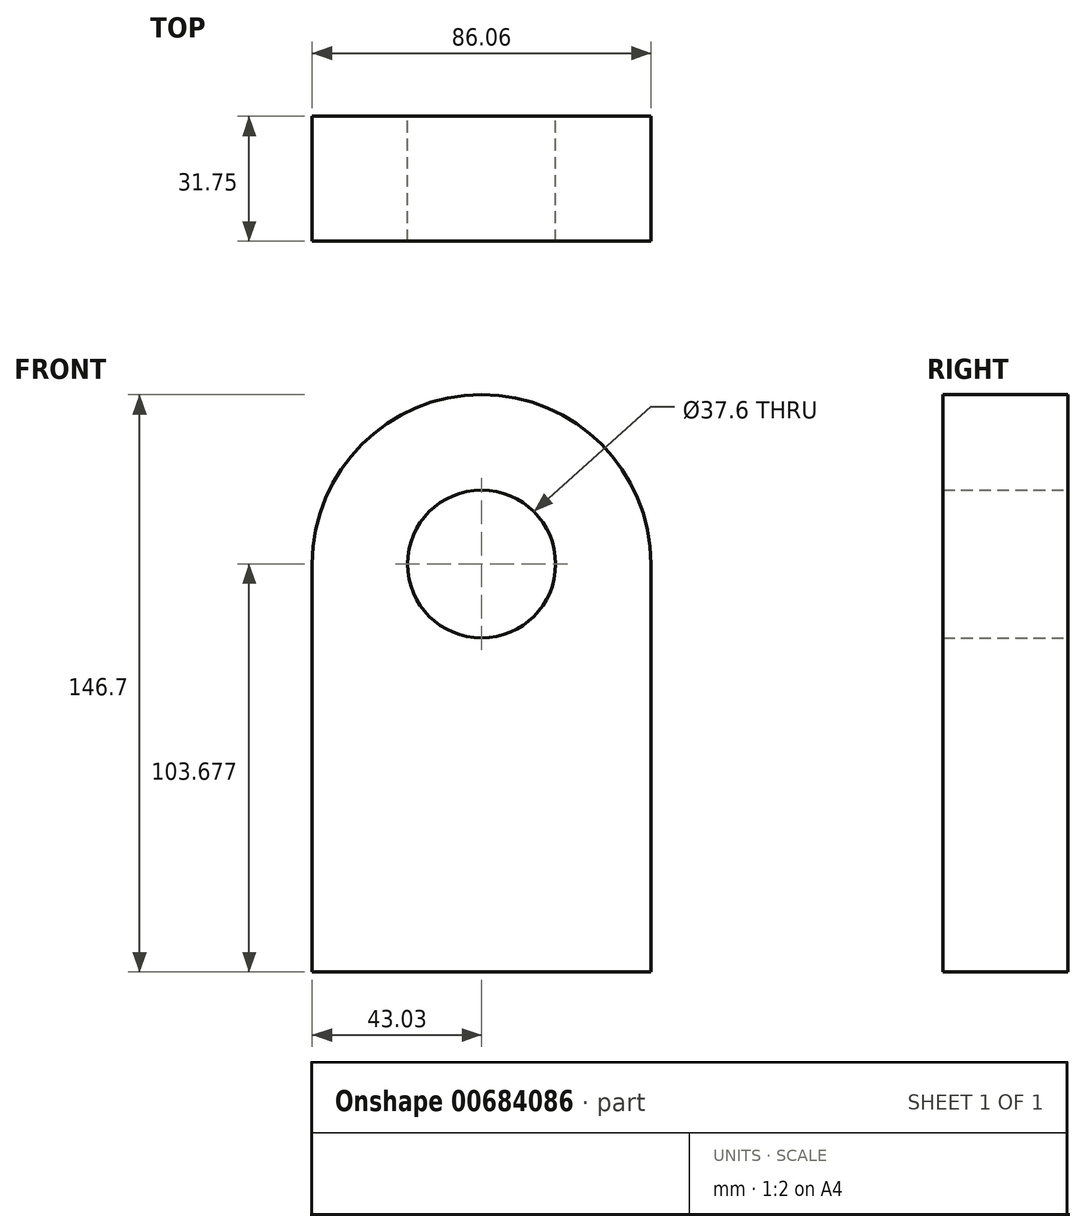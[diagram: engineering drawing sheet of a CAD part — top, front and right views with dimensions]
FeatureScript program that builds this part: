
annotation { "Feature Type Name" : "Feature", "Feature Type Description" : "" }
export const myFeature = defineFeature(function(context is Context, id is Id, definition is map)
    precondition{}
    {
        {
            var Q0;
            Q0=qCreatedBy(makeId("Front.planeOp"),FACE);
            var sketch = newSketch(context, id + "F0", { "sketchPlane" : qUnion([Q0])});
            skLineSegment(sketch, "E0.top", {"start": v(43.03, -51.84) * mm, "end": v(-43.03, -51.84) * mm});
            skLineSegment(sketch, "E0.left", {"start": v(43.03, 51.84) * mm, "end": v(43.03, -51.84) * mm});
            skLineSegment(sketch, "E0.right", {"start": v(-43.03, 51.84) * mm, "end": v(-43.03, -51.84) * mm});
            skPoint(sketch, "E0.middle", {"position": v(0, 0) * mm});
            skArc(sketch, "E1", {"start": v(43.03, 51.84) * mm, "mid": v(0, 94.86) * mm, "end": v(-43.03, 51.84) * mm});
            skCircle(sketch, "E2", {"center": v(0, 51.84) * mm, "radius": 18.8 * mm});
            skSolve(sketch);
        }
        {
            var Q0;
            Q0=makeQuery(id+"F0.imprint","IMPRINT",FACE,{"disambiguationData":[TD([[makeQuery(id+"F0.imprint","IMPRINT",EDGE,{"derivedFrom":sQuery(id+"F0.wireOp",EDGE,"E0.top")}),-1.0]])]});
            extrude(context, id + "F1", {"entities" : qUnion([Q0]), "depth" : 31.75 * mm, "offsetDistance" : 25.4 * mm});
        }
    });
